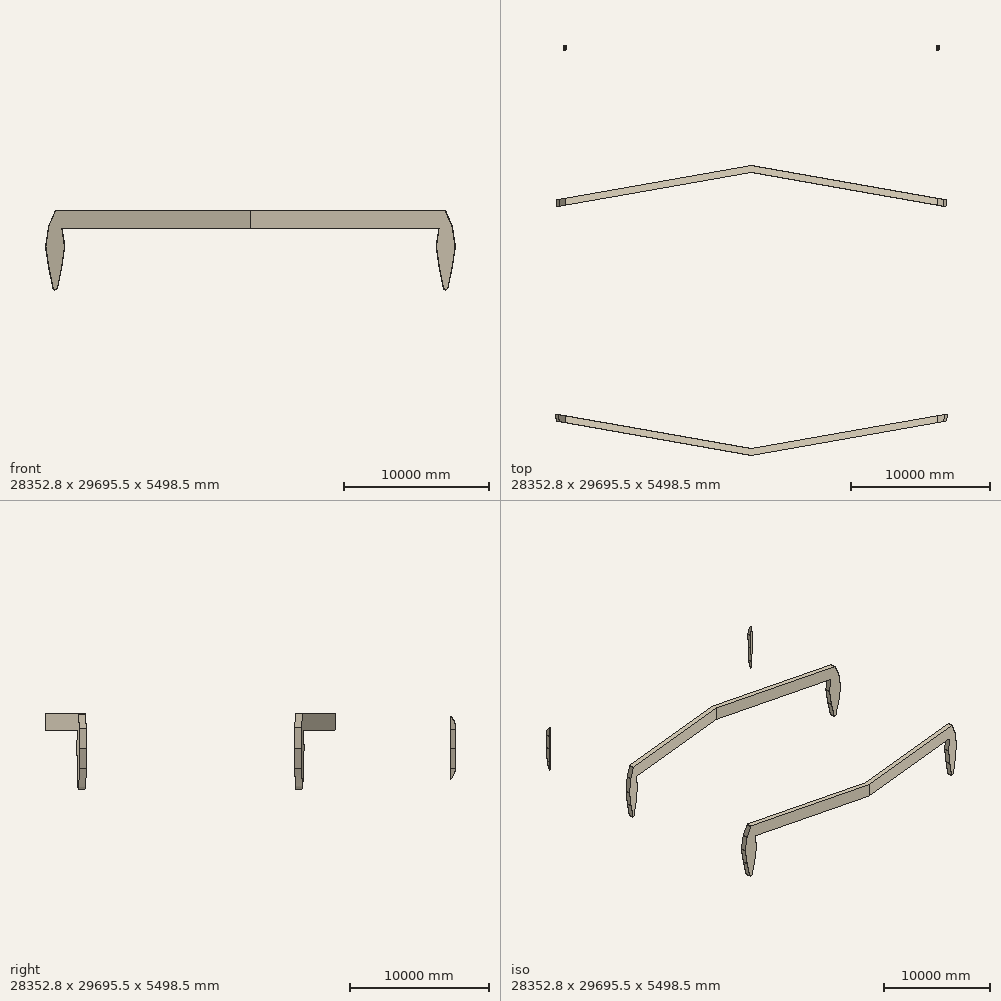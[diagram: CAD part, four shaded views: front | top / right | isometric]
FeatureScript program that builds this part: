
annotation { "Feature Type Name" : "Feature", "Feature Type Description" : "" }
export const myFeature = defineFeature(function(context is Context, id is Id, definition is map)
    precondition{}
    {
        {
            var Q0;
            Q0=qCreatedBy(makeId("Front.planeOp"),FACE);
            var sketch = newSketch(context, id + "F0", { "sketchPlane" : qUnion([Q0])});
            skPoint(sketch, "E0.end.orphan", {"position": v(0, 0) * mm});
            skLineSegment(sketch, "E1", {"start": v(0, 0) * mm, "end": v(0, -5500) * mm});
            skLineSegment(sketch, "E2", {"start": v(500, -4000) * mm, "end": v(750, -2500) * mm});
            skFitSpline(sketch, "E3", {"points": [v(0, -5500) * mm, v(189.72, -5319.94) * mm, v(366.95, -4555.93) * mm, v(500, -4000) * mm], "startDerivative": vector(1833.22, 785.24) * mm, "endDerivative": vector(535.36, 2334.8) * mm});
            skLineSegment(sketch, "E4", {"start": v(0, 0) * mm, "end": v(500, -1000) * mm});
            skLineSegment(sketch, "E5", {"start": v(500, -1000) * mm, "end": v(750, -2500) * mm});
            skSolve(sketch);
        }
        {
            var Q0;
            Q0=qCreatedBy(makeId("Front.planeOp"),FACE);
            cPlane(context, id + "F1", {"entities" : qUnion([Q0]), "cplaneType" : CPlaneType.OFFSET, "offset" : 10000 * mm, "oppositeDirection" : true, "width" : 150 * mm, "height" : 150 * mm});
        }
        {
            var Q0;
            Q0=qCreatedBy(id+"F1.planeOp",FACE);
            var sketch = newSketch(context, id + "F2", { "sketchPlane" : qUnion([Q0])});
            skLineSegment(sketch, "E6", {"start": v(0, 0) * mm, "end": v(0, -5500) * mm});
            skFitSpline(sketch, "E7", {"points": [v(0, -5500) * mm, v(174.15, -5265.2) * mm, v(305.11, -4690.98) * mm, v(500, -4000) * mm], "startDerivative": vector(1750.56, 1279.5) * mm, "endDerivative": vector(993.95, 3484.4) * mm});
            skLineSegment(sketch, "E8", {"start": v(500, -4000) * mm, "end": v(750, -2500) * mm});
            skPoint(sketch, "E9.startDerivative.orphan", {"position": v(5091.83, 0) * mm});
            skLineSegment(sketch, "E10", {"start": v(500, -1000) * mm, "end": v(0, 0) * mm});
            skLineSegment(sketch, "E11", {"start": v(750, -2500) * mm, "end": v(500, -1000) * mm});
            skSolve(sketch);
        }
        {
            var Q0;
            Q0=qCreatedBy(id+"F1.planeOp",FACE);
            cPlane(context, id + "F3", {"entities" : qUnion([Q0]), "cplaneType" : CPlaneType.OFFSET, "offset" : 15000 * mm, "oppositeDirection" : true, "width" : 150 * mm, "height" : 150 * mm});
        }
        {
            var Q0;
            Q0=qCreatedBy(id+"F3.planeOp",FACE);
            var sketch = newSketch(context, id + "F4", { "sketchPlane" : qUnion([Q0])});
            skLineSegment(sketch, "E12", {"start": v(0, 0) * mm, "end": v(0, -5500) * mm});
            skLineSegment(sketch, "E13", {"start": v(0, -5500) * mm, "end": v(0, -5500) * mm});
            skLineSegment(sketch, "E14", {"start": v(0, -5500) * mm, "end": v(12.9, -4000) * mm});
            skLineSegment(sketch, "E15", {"start": v(12.9, -4000) * mm, "end": v(85.66, -2500) * mm});
            skLineSegment(sketch, "E16", {"start": v(0, 0) * mm, "end": v(94.2, -1134.32) * mm});
            skLineSegment(sketch, "E17", {"start": v(94.2, -1134.32) * mm, "end": v(85.66, -2500) * mm});
            skSolve(sketch);
        }
        {
            var Q0;
            Q0=qCreatedBy(makeId("Front.planeOp"),FACE);
            cPlane(context, id + "F5", {"entities" : qUnion([Q0]), "cplaneType" : CPlaneType.OFFSET, "offset" : 10000 * mm, "width" : 150 * mm, "height" : 150 * mm});
        }
        {
            var Q0;
            Q0=qCreatedBy(id+"F5.planeOp",FACE);
            var sketch = newSketch(context, id + "F6", { "sketchPlane" : qUnion([Q0])});
            skLineSegment(sketch, "E18", {"start": v(0, -500) * mm, "end": v(0, -5500) * mm});
            skLineSegment(sketch, "E19", {"start": v(0, -5500) * mm, "end": v(14.37, -4000) * mm});
            skLineSegment(sketch, "E20", {"start": v(14.37, -4000) * mm, "end": v(85.96, -2500) * mm});
            skPoint(sketch, "E21", {"position": v(51.72, -1902.5) * mm});
            skLineSegment(sketch, "E22", {"start": v(94.34, -1565.05) * mm, "end": v(85.96, -2500) * mm});
            skLineSegment(sketch, "E23", {"start": v(0, -500) * mm, "end": v(94.34, -1565.05) * mm});
            skSolve(sketch);
        }
        {
            var Q0;
            Q0=makeQuery(id+"F4.imprint","IMPRINT",FACE,{"disambiguationData":[TD([[makeQuery(id+"F4.imprint","IMPRINT",EDGE,{"derivedFrom":sQuery(id+"F4.wireOp",EDGE,"E12")}),1.0]])]});
            var Q1;
            Q1=makeQuery(id+"F2.imprint","IMPRINT",FACE,{"disambiguationData":[TD([[makeQuery(id+"F2.imprint","IMPRINT",EDGE,{"derivedFrom":sQuery(id+"F2.wireOp",EDGE,"E6")}),1.0]])]});
            var Q2;
            Q2=makeQuery(id+"F0.imprint","IMPRINT",FACE,{"disambiguationData":[TD([[makeQuery(id+"F0.imprint","IMPRINT",EDGE,{"derivedFrom":sQuery(id+"F0.wireOp",EDGE,"E1")}),1.0]])]});
            var Q3;
            Q3=makeQuery(id+"F6.imprint","IMPRINT",FACE,{"disambiguationData":[TD([[makeQuery(id+"F6.imprint","IMPRINT",EDGE,{"derivedFrom":sQuery(id+"F6.wireOp",EDGE,"E18")}),1.0]])]});
            var Q4;
            Q4=sQuery(id+"F4.wireOp",EDGE,"E14");
            var Q5;
            Q5=sQuery(id+"F2.wireOp",EDGE,"E8");
            var Q6;
            Q6=sQuery(id+"F4.wireOp",EDGE,"E15");
            var Q7;
            Q7=sQuery(id+"F4.wireOp",EDGE,"sgJCfSwm-QjFF-VmRN-4AcW-iuittDDyERBM");
            loft(context, id + "F7", {"sheetProfilesArray" : [{ "sheetProfileEntities" : qUnion([Q0]) }, { "sheetProfileEntities" : qUnion([Q1]) }, { "sheetProfileEntities" : qUnion([Q2]) }, { "sheetProfileEntities" : qUnion([Q3]) }], "guidesArray" : [{ "guideEntities" : qUnion([Q4]), "guideDerivativeType" : LoftGuideDerivativeType.DEFAULT, "guideDerivativeMagnitude" : 1 }, { "guideEntities" : qUnion([Q5]), "guideDerivativeType" : LoftGuideDerivativeType.DEFAULT, "guideDerivativeMagnitude" : 1 }, { "guideEntities" : qUnion([Q6]), "guideDerivativeType" : LoftGuideDerivativeType.DEFAULT, "guideDerivativeMagnitude" : 1 }, { "guideEntities" : qUnion([Q7]), "guideDerivativeType" : LoftGuideDerivativeType.DEFAULT, "guideDerivativeMagnitude" : 1 }]});
        }
        {
            var Q0;
            Q0=makeQuery(id+"F7.opLoft","SWEPT_BODY",BODY,{"disambiguationData":[OSD([sQuery(id+"F0.wireOp",EDGE,"E3"),sQuery(id+"F2.wireOp",EDGE,"E7"),makeQuery(id+"F4.imprint","IMPRINT",FACE,{"disambiguationData":[TD([[makeQuery(id+"F4.imprint","IMPRINT",EDGE,{"derivedFrom":sQuery(id+"F4.wireOp",EDGE,"E12")}),1.0]])]}),makeQuery(id+"F6.imprint","IMPRINT",FACE,{"disambiguationData":[TD([[makeQuery(id+"F6.imprint","IMPRINT",EDGE,{"derivedFrom":sQuery(id+"F6.wireOp",EDGE,"E18")}),1.0]])]})])]});
            var Q1;
            Q1=qCreatedBy(makeId("Right.planeOp"),FACE);
            mirror(context, id + "F8", {"operationType" : NewBodyOperationType.ADD, "entities" : qUnion([Q0]), "mirrorPlane" : qUnion([Q1])});
        }
        {
            var Q0;
            {var subQ0=makeQuery(id+"F7.opLoft","SWEPT_EDGE",EDGE,{"disambiguationData":[OSD([sQuery(id+"F0.wireOp",EDGE,"E1"),sQuery(id+"F0.wireOp",EDGE,"E3"),sQuery(id+"F6.wireOp",EDGE,"E18"),sQuery(id+"F6.wireOp",EDGE,"E19")])]});Q0=makeQuery(id+"F8.boolean.opBoolean","MERGE",EDGE,{"derivedFrom":[subQ0,makeQuery(id+"F8.opPattern","COPY",EDGE,{"derivedFrom":subQ0,"instanceName":"1"})]});}
            fillet(context, id + "F9", {"entities" : qUnion([Q0]), "radius" : 12 * mm, "tangentPropagation" : true, "allowEdgeOverflow" : false});
        }
        {
            var Q0;
            Q0=qCreatedBy(makeId("Front.planeOp"),FACE);
            var sketch = newSketch(context, id + "F10", { "sketchPlane" : qUnion([Q0])});
            skLineSegment(sketch, "E24", {"start": v(0, 0) * mm, "end": v(0, -5082.07) * mm, "construction": true});
            skLineSegment(sketch, "E25", {"start": v(-7000, 3102.27) * mm, "end": v(-7000, -5771.46) * mm, "construction": true});
            skLineSegment(sketch, "E26", {"start": v(-7000, 0) * mm, "end": v(-13500, 0) * mm});
            skLineSegment(sketch, "E27", {"start": v(-13500, 0) * mm, "end": v(-13500, -1000) * mm});
            skLineSegment(sketch, "E28", {"start": v(-13500, -1000) * mm, "end": v(-7000, -1000) * mm});
            skLineSegment(sketch, "E29", {"start": v(-7000, -1000) * mm, "end": v(0, -1000) * mm});
            skLineSegment(sketch, "E30", {"start": v(0, 0) * mm, "end": v(0, -1000) * mm});
            skLineSegment(sketch, "E31", {"start": v(-7000, 0) * mm, "end": v(0, 0) * mm});
            skSolve(sketch);
        }
        {
            var Q0;
            Q0=makeQuery(id+"F10.imprint","IMPRINT",FACE,{"disambiguationData":[TD([[makeQuery(id+"F10.imprint","IMPRINT",EDGE,{"derivedFrom":sQuery(id+"F10.wireOp",EDGE,"3sFQAXWc-wyO7-hPk9-7dSX-oAIZwABY1ojd")}),1.0]])]});
            var Q1;
            Q1=makeQuery(id+"F10.imprint","IMPRINT",FACE,{"disambiguationData":[TD([[makeQuery(id+"F10.imprint","IMPRINT",EDGE,{"derivedFrom":sQuery(id+"F10.wireOp",EDGE,"E26")}),1.0]])]});
            extrude(context, id + "F11", {"entities" : qUnion([Q0, Q1]), "oppositeDirection" : true, "depth" : 37400 * mm, "symmetric" : true});
        }
        {
            var Q0;
            Q0=qCreatedBy(makeId("Top.planeOp"),FACE);
            var sketch = newSketch(context, id + "F12", { "sketchPlane" : qUnion([Q0])});
            skLineSegment(sketch, "E32.bottom", {"start": v(-13500, 24621.28) * mm, "end": v(7276.55, 24621.28) * mm});
            skLineSegment(sketch, "E32.left", {"start": v(-13500, 24621.28) * mm, "end": v(-13500, 16304.47) * mm});
            skLineSegment(sketch, "E32.right", {"start": v(7276.55, 24621.28) * mm, "end": v(7276.55, 18829) * mm});
            skLineSegment(sketch, "E33.left", {"start": v(-13500, 15804.47) * mm, "end": v(-13500, -4195.53) * mm});
            skLineSegment(sketch, "E33.right", {"start": v(8153.2, 18329) * mm, "end": v(8153.2, -1671) * mm});
            skLineSegment(sketch, "E34.top", {"start": v(-13500, -21040.08) * mm, "end": v(8250.14, -21040.08) * mm});
            skLineSegment(sketch, "E34.left", {"start": v(-13500, -4695.53) * mm, "end": v(-13500, -21040.08) * mm});
            skLineSegment(sketch, "E34.right", {"start": v(8250.14, -2171) * mm, "end": v(8250.14, -21040.08) * mm});
            skLineSegment(sketch, "E35", {"start": v(0, -1047.14) * mm, "end": v(-1927.45, -1047.14) * mm, "construction": true});
            skLineSegment(sketch, "E36", {"start": v(0, 2086.97) * mm, "end": v(-2089.7, 2086.97) * mm, "construction": true});
            skLineSegment(sketch, "E37", {"start": v(-13500, 23613.23) * mm, "end": v(-13500, -27703.45) * mm, "construction": true});
            skLineSegment(sketch, "E38", {"start": v(-13500, 16304.47) * mm, "end": v(8153.2, 12486.43) * mm});
            skLineSegment(sketch, "E39", {"start": v(-13500, 15804.47) * mm, "end": v(8153.2, 11986.43) * mm});
            skLineSegment(sketch, "E40", {"start": v(-13500, -4195.53) * mm, "end": v(8153.2, -377.49) * mm});
            skLineSegment(sketch, "E41", {"start": v(-13500, -4695.53) * mm, "end": v(8153.2, -877.49) * mm});
            skLineSegment(sketch, "E42", {"start": v(7276.55, 18829) * mm, "end": v(8153.2, 18329) * mm});
            skLineSegment(sketch, "E43", {"start": v(8153.2, -1671) * mm, "end": v(8250.14, -2171) * mm});
            skSolve(sketch);
        }
        {
            var Q0;
            Q0=makeQuery(id+"F12.imprint","IMPRINT",FACE,{"disambiguationData":[TD([[makeQuery(id+"F12.imprint","IMPRINT",EDGE,{"derivedFrom":sQuery(id+"F12.wireOp",EDGE,"E32.bottom")}),-1.0]])]});
            var Q1;
            Q1=makeQuery(id+"F12.imprint","IMPRINT",FACE,{"disambiguationData":[TD([[makeQuery(id+"F12.imprint","IMPRINT",EDGE,{"derivedFrom":sQuery(id+"F12.wireOp",EDGE,"E33.left")}),1.0]])]});
            var Q2;
            Q2=makeQuery(id+"F12.imprint","IMPRINT",FACE,{"disambiguationData":[TD([[makeQuery(id+"F12.imprint","IMPRINT",EDGE,{"derivedFrom":sQuery(id+"F12.wireOp",EDGE,"E34.top")}),1.0]])]});
            extrude(context, id + "F13", {"entities" : qUnion([Q0, Q1, Q2]), "operationType" : NewBodyOperationType.REMOVE, "oppositeDirection" : true, "depth" : 13225 * mm, "symmetric" : true});
        }
        {
            var Q0;
            Q0=makeQuery(id+"F7.opLoft","SWEPT_BODY",BODY,{"disambiguationData":[OSD([sQuery(id+"F0.wireOp",EDGE,"E4"),sQuery(id+"F2.wireOp",EDGE,"E8"),makeQuery(id+"F4.imprint","IMPRINT",FACE,{"disambiguationData":[TD([[makeQuery(id+"F4.imprint","IMPRINT",EDGE,{"derivedFrom":sQuery(id+"F4.wireOp",EDGE,"E12")}),1.0]])]}),makeQuery(id+"F6.imprint","IMPRINT",FACE,{"disambiguationData":[TD([[makeQuery(id+"F6.imprint","IMPRINT",EDGE,{"derivedFrom":sQuery(id+"F6.wireOp",EDGE,"E18")}),1.0]])]})])]});
            var Q1;
            Q1=makeQuery(id+"F11.opExtrude","SWEPT_BODY",BODY,{"disambiguationData":[OSD([sQuery(id+"F10.wireOp",EDGE,"E26"),sQuery(id+"F10.wireOp",EDGE,"E27"),sQuery(id+"F10.wireOp",EDGE,"E28"),sQuery(id+"F10.wireOp",EDGE,"E29"),sQuery(id+"F10.wireOp",EDGE,"E30"),sQuery(id+"F10.wireOp",EDGE,"E31")])]});
            var Q2;
            Q2=makeQuery(id+"F11.opExtrude","SWEPT_FACE",FACE,{"disambiguationData":[OSD([sQuery(id+"F10.wireOp",EDGE,"E27")])]});
            mirror(context, id + "F14", {"operationType" : NewBodyOperationType.ADD, "entities" : qUnion([Q0, Q1]), "mirrorPlane" : qUnion([Q2])});
        }
        {
            var Q0;
            Q0=qCreatedBy(makeId("Right.planeOp"),FACE);
            var sketch = newSketch(context, id + "F15", { "sketchPlane" : qUnion([Q0])});
            skLineSegment(sketch, "E44", {"start": v(25015.3, -3553.39) * mm, "end": v(25015.3, -1000) * mm});
            skLineSegment(sketch, "E45", {"start": v(24015.3, 0) * mm, "end": v(13594.14, 0) * mm});
            skLineSegment(sketch, "E46", {"start": v(13594.14, 0) * mm, "end": v(12052.37, 3741.26) * mm});
            skLineSegment(sketch, "E47", {"start": v(12052.37, 3741.26) * mm, "end": v(25847.84, 3035.2) * mm});
            skLineSegment(sketch, "E48", {"start": v(25847.84, 3035.2) * mm, "end": v(26929.87, 1249.84) * mm});
            skLineSegment(sketch, "E49", {"start": v(26929.87, 1249.84) * mm, "end": v(25015.3, -3553.39) * mm});
            skPoint(sketch, "E50.visualSharp", {"position": v(25015.3, 0) * mm});
            skArc(sketch, "E50.filletArc", {"start": v(25015.3, -1000) * mm, "mid": v(24722.4, -292.9) * mm, "end": v(24015.3, 0) * mm});
            skLineSegment(sketch, "E51", {"start": v(-10015.9, -1415.8) * mm, "end": v(-10015.9, -3965.22) * mm});
            skLineSegment(sketch, "E52", {"start": v(-10015.9, -3965.22) * mm, "end": v(-12936.5, -3419.61) * mm});
            skLineSegment(sketch, "E53", {"start": v(-12936.5, -3419.61) * mm, "end": v(-12936.5, 1047.72) * mm});
            skLineSegment(sketch, "E54", {"start": v(-12936.5, 1047.72) * mm, "end": v(-5974.96, 1396.63) * mm});
            skPoint(sketch, "E55.visualSharp", {"position": v(-10015.9, 0) * mm});
            skPoint(sketch, "E56.visualSharp", {"position": v(-10015.9, -509.7) * mm});
            skArc(sketch, "E56.filletArc", {"start": v(-9114.2, -420.64) * mm, "mid": v(-9756.95, -744.34) * mm, "end": v(-10015.9, -1415.8) * mm});
            skLineSegment(sketch, "E57", {"start": v(-5974.96, 1396.63) * mm, "end": v(-4930.65, -171.54) * mm});
            skLineSegment(sketch, "E58", {"start": v(-4930.65, -171.54) * mm, "end": v(-9114.2, -420.64) * mm});
            skSolve(sketch);
        }
        {
            var Q0;
            Q0=makeQuery(id+"F15.imprint","IMPRINT",FACE,{"disambiguationData":[TD([[makeQuery(id+"F15.imprint","IMPRINT",EDGE,{"derivedFrom":sQuery(id+"F15.wireOp",EDGE,"E51")}),-1.0]])]});
            var Q1;
            Q1=makeQuery(id+"F15.imprint","IMPRINT",FACE,{"disambiguationData":[TD([[makeQuery(id+"F15.imprint","IMPRINT",EDGE,{"derivedFrom":sQuery(id+"F15.wireOp",EDGE,"E44")}),-1.0]])]});
            extrude(context, id + "F16", {"entities" : qUnion([Q0, Q1]), "operationType" : NewBodyOperationType.REMOVE, "oppositeDirection" : true, "depth" : 88000 * mm, "symmetric" : true});
        }
        {
            var Q0;
            {var subQ0=makeQuery(id+"F13.boolean.opBoolean","SPLIT",FACE,{"disambiguationData":[TD([makeQuery(id+"F13.opExtrude","SWEPT_FACE",FACE,{"disambiguationData":[OSD([sQuery(id+"F12.wireOp",EDGE,"E40")])]})])],"derivedFrom":makeQuery(id+"F11.opExtrude","SWEPT_FACE",FACE,{"disambiguationData":[OSD([sQuery(id+"F10.wireOp",EDGE,"E28"),sQuery(id+"F10.wireOp",EDGE,"E29")])]})});Q0=makeQuery(id+"F14.boolean.opBoolean","MERGE",FACE,{"derivedFrom":[subQ0,makeQuery(id+"F14.opPattern","COPY",FACE,{"derivedFrom":subQ0,"instanceName":"1"})]});}
            var Q1;
            {var subQ0=makeQuery(id+"F13.boolean.opBoolean","SPLIT",FACE,{"disambiguationData":[TD([makeQuery(id+"F13.opExtrude","SWEPT_FACE",FACE,{"disambiguationData":[OSD([sQuery(id+"F12.wireOp",EDGE,"E38")])]})])],"derivedFrom":makeQuery(id+"F11.opExtrude","SWEPT_FACE",FACE,{"disambiguationData":[OSD([sQuery(id+"F10.wireOp",EDGE,"E28"),sQuery(id+"F10.wireOp",EDGE,"E29")])]})});Q1=makeQuery(id+"F14.boolean.opBoolean","MERGE",FACE,{"derivedFrom":[subQ0,makeQuery(id+"F14.opPattern","COPY",FACE,{"derivedFrom":subQ0,"instanceName":"1"})]});}
            extrude(context, id + "F17", {"entities" : qUnion([Q0, Q1]), "operationType" : NewBodyOperationType.ADD, "depth" : 250 * mm});
        }
    });
